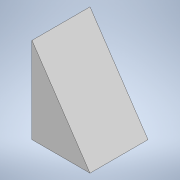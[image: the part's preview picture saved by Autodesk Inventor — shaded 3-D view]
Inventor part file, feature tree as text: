
AUTODESK INVENTOR PART (.ipt)
format: ipt  version: 2022 (Build 260153000, 153)  size: 88,064 bytes
history: native  units: mm
features: other x1, extrude x1, sketch x1
ambient origin geometry x8: Origin, YZ Plane, XZ Plane, XY Plane, X Axis, Y Axis, Z Axis, Center Point
bodies: Body1 (feature_tree)
feature tree (3):
  other  "Твердое тело1"
  extrude  "Выдавливание1"  Depth=10.0mm
  sketch  "Эскиз1"
